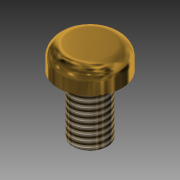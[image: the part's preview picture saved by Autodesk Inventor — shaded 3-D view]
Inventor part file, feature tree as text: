
AUTODESK INVENTOR PART (.ipt)
format: ipt  version: 2015 (Build 190159000, 159)  size: 129,536 bytes
history: native  units: mm
features: extrude x2, sketch x2, other x1, fillet x1, thread x1
ambient origin geometry x8: Origin, YZ Plane, XZ Plane, XY Plane, X Axis, Y Axis, Z Axis, Center Point
bodies: Body1 (feature_tree)
feature tree (7):
  other  "ソリッド1"
  extrude  "押し出し1"  Depth=5.5mm
  fillet  "フィレット1"  Radius=2.0mm
  extrude  "押し出し2"  Depth=1.0mm
  thread  "ねじ1"
  sketch  "スケッチ1"
  sketch  "スケッチ2"
